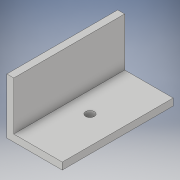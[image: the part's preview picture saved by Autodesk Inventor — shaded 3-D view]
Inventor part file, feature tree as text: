
AUTODESK INVENTOR PART (.ipt)
format: ipt  version: 2018 (Build 220112000, 112)  size: 106,496 bytes
history: native  units: in
note: dims shown in document units (in); Inventor stores cm internally (conversion verified against a paired STEP export)
features: extrude x2, sketch x2
ambient origin geometry x8: Origin, YZ Plane, XZ Plane, XY Plane, X Axis, Y Axis, Z Axis, Center Point
bodies: Solid1 (feature_tree)
feature tree (4):
  extrude  "Extrusion1"  Depth=1.0in
  extrude  "Extrusion2"  Depth=0.125in
  sketch  "Sketch1"  dims[d0=0.125in d1=1.0in]
  sketch  "Sketch2"  dims[d2=1.0in d3=0.125in d4=2.0in d5=0.0in d6=0.5in d7=1.0in d8=0.1562in d9=2.0in d10=0.0in]
